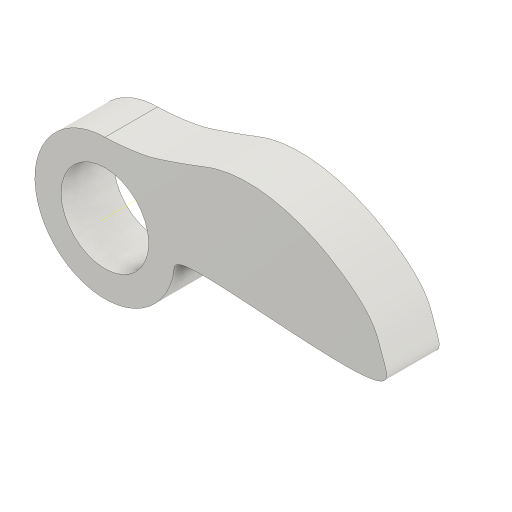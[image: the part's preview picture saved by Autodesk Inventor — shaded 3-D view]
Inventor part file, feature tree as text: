
AUTODESK INVENTOR PART (.ipt)
format: ipt  version: 2023.3 (Build 273359000, 359)  size: 118,784 bytes
history: native  units: mm (DEFAULTED — no unit token found)
features: extrude x1, hole x1, other x1, sketch x1
ambient origin geometry x8: Origin, YZ Plane, XZ Plane, XY Plane, X Axis, Y Axis, Z Axis, Center Point
bodies: Solid1 (feature_tree)
feature tree (4):
  extrude  "Nocken"  TaperAngle=0.0deg  [1 undecoded]
  hole  "Bohrung1"  [1 undecoded]
  other  "Hauptskizze"
  sketch  "Skizze2"  dims[d1=0.0mm d2=0.0mm d3=0.0mm d4=5.0mm d5=6.0mm d6=4.0mm d7=2.0mm d8=90.0deg d9=8.8mm d10=0.0mm]
note: 2 required parameter values undecoded (feature->parameter linkage not recoverable at this tier; creation-order binding heuristic only, values carry confidence <= 0.55)
